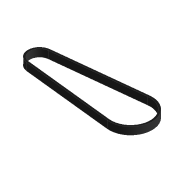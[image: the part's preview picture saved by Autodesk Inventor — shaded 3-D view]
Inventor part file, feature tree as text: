
AUTODESK INVENTOR PART (.ipt)
format: ipt  version: 2022.5 (Build 265521000, 521)  size: 94,208 bytes
history: native  units: mm
features: sweep x1, sketch x1
ambient origin geometry x8: Origin, YZ Plane, XZ Plane, XY Plane, X Axis, Y Axis, Z Axis, Center Point
bodies: Body1 (feature_tree)
feature tree (2):
  sweep  "Sweep1"
  sketch  "Sketch3"  dims[d0=74.5mm d2=16.0mm d8=32.0mm d9=1.5mm d10=6.0mm d11=8.0mm d12=0.0mm d13=0.0mm]
